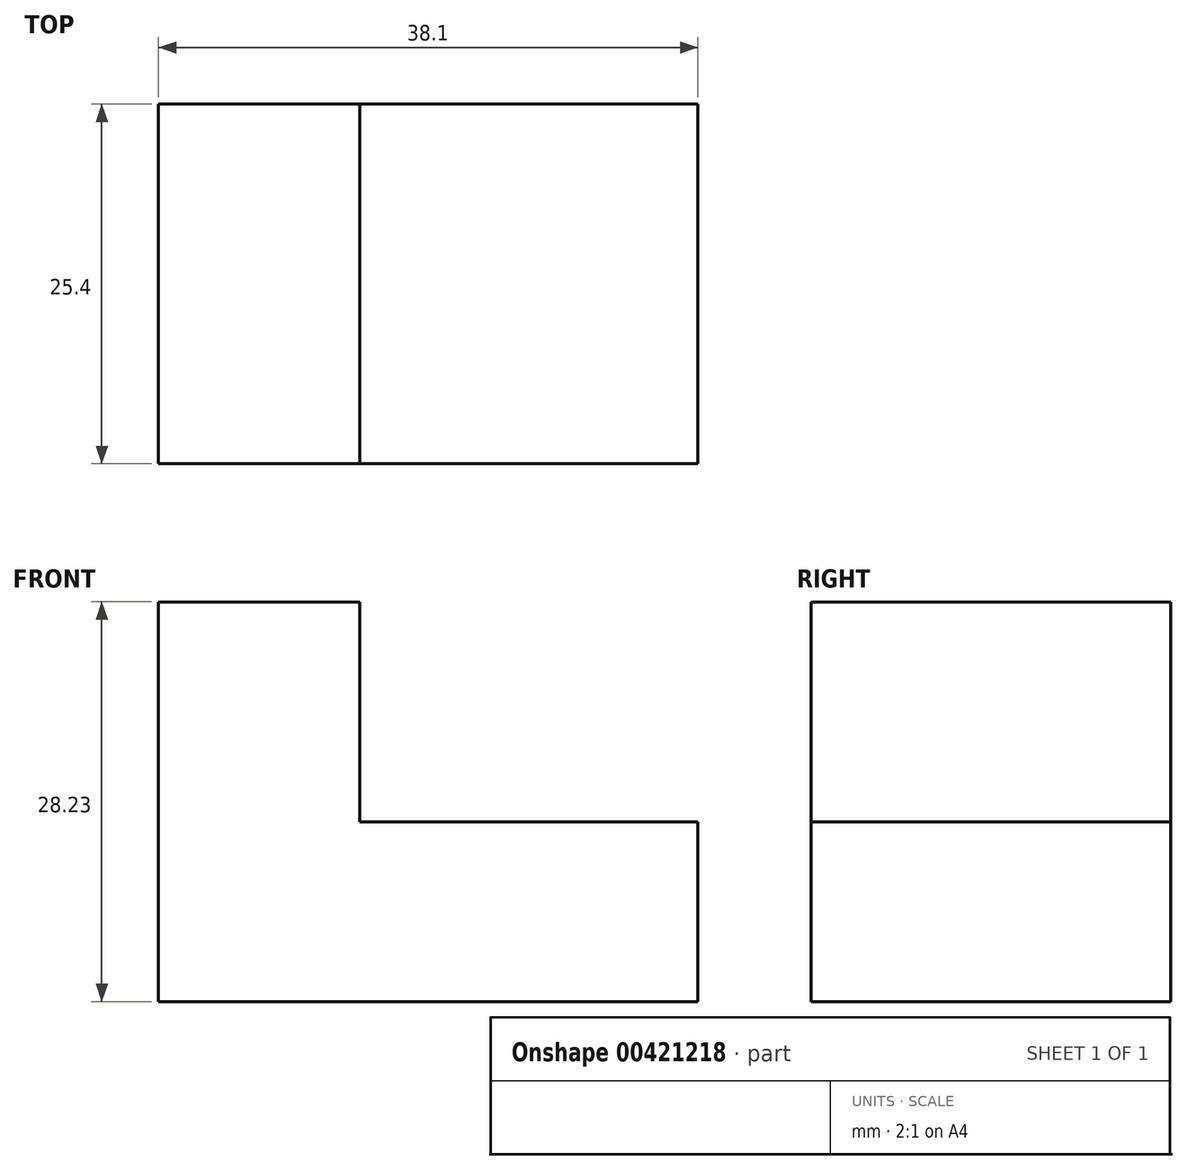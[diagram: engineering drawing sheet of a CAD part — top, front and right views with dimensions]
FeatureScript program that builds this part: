
annotation { "Feature Type Name" : "Feature", "Feature Type Description" : "" }
export const myFeature = defineFeature(function(context is Context, id is Id, definition is map)
    precondition{}
    {
        {
            var Q0;
            Q0=qCreatedBy(makeId("Front.planeOp"),FACE);
            var sketch = newSketch(context, id + "F0", { "sketchPlane" : qUnion([Q0])});
            skLineSegment(sketch, "E0", {"start": v(0, 0) * mm, "end": v(38.1, 0) * mm});
            skLineSegment(sketch, "E1", {"start": v(38.1, 0) * mm, "end": v(38.1, 12.7) * mm});
            skLineSegment(sketch, "E2", {"start": v(38.1, 12.7) * mm, "end": v(14.21, 12.7) * mm});
            skLineSegment(sketch, "E3", {"start": v(14.21, 12.7) * mm, "end": v(14.21, 28.23) * mm});
            skLineSegment(sketch, "E4", {"start": v(14.21, 28.23) * mm, "end": v(0, 28.23) * mm});
            skLineSegment(sketch, "E5", {"start": v(0, 28.23) * mm, "end": v(0, 0) * mm});
            skSolve(sketch);
        }
        {
            var Q0;
            Q0=makeQuery(id+"F0.imprint","IMPRINT",FACE,{"disambiguationData":[TD([[makeQuery(id+"F0.imprint","IMPRINT",EDGE,{"derivedFrom":sQuery(id+"F0.wireOp",EDGE,"E0")}),1.0]])]});
            extrude(context, id + "F1", {"entities" : qUnion([Q0]), "depth" : 25.4 * mm});
        }
    });
